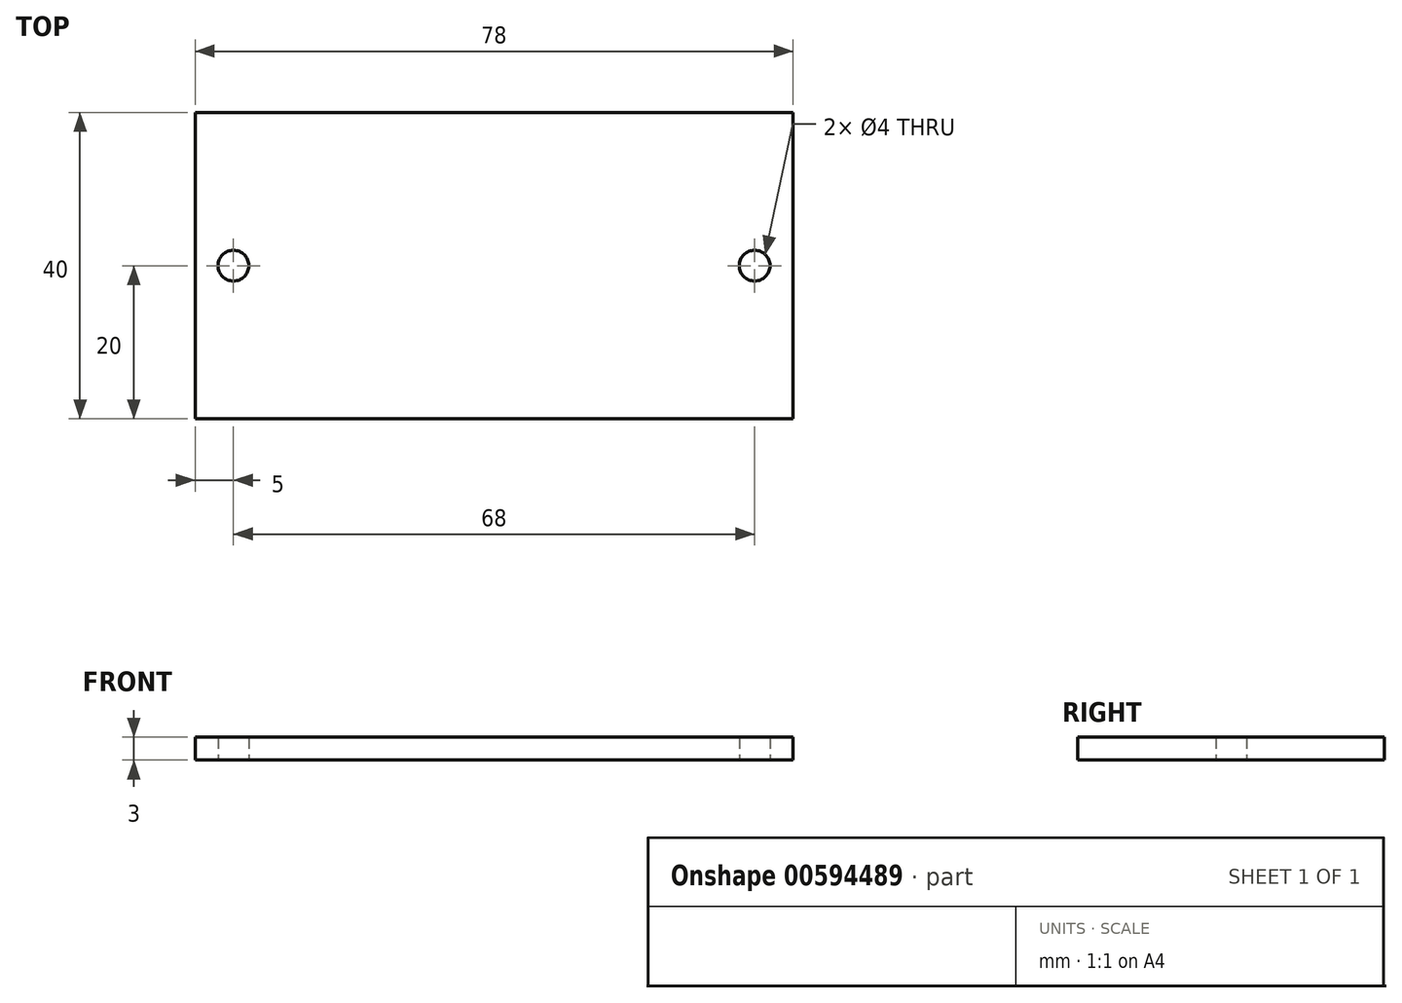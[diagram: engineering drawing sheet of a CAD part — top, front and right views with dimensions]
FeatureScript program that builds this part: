
annotation { "Feature Type Name" : "Feature", "Feature Type Description" : "" }
export const myFeature = defineFeature(function(context is Context, id is Id, definition is map)
    precondition{}
    {
        {
            var Q0;
            Q0=qCreatedBy(makeId("Top.planeOp"),FACE);
            var sketch = newSketch(context, id + "F0", { "sketchPlane" : qUnion([Q0])});
            skLineSegment(sketch, "E0", {"start": v(0, 40) * mm, "end": v(-39, 40) * mm});
            skLineSegment(sketch, "E1", {"start": v(-39, 40) * mm, "end": v(-39, 0) * mm});
            skLineSegment(sketch, "E2", {"start": v(-39, 0) * mm, "end": v(0, 0) * mm});
            skLineSegment(sketch, "E3", {"start": v(0, 40) * mm, "end": v(0, 0) * mm});
            skCircle(sketch, "E4", {"center": v(-34, 20) * mm, "radius": 2 * mm});
            skPoint(sketch, "E4.centerSnap0", {"position": v(-39, 20) * mm});
            skLineSegment(sketch, "E5.MirrorCS", {"start": v(0, 40) * mm, "end": v(39, 40) * mm});
            skLineSegment(sketch, "E6.MirrorCS", {"start": v(39, 40) * mm, "end": v(39, 0) * mm});
            skCircle(sketch, "E7.MirrorC", {"center": v(34, 20) * mm, "radius": 2 * mm});
            skLineSegment(sketch, "E8.MirrorCS", {"start": v(39, 0) * mm, "end": v(0, 0) * mm});
            skSolve(sketch);
        }
        {
            var Q0;
            Q0 = qSketchRegion(id + "F0", true);
            extrude(context, id + "F1", {"entities" : qUnion([Q0]), "depth" : 3 * mm, "offsetDistance" : 25 * mm});
        }
    });
